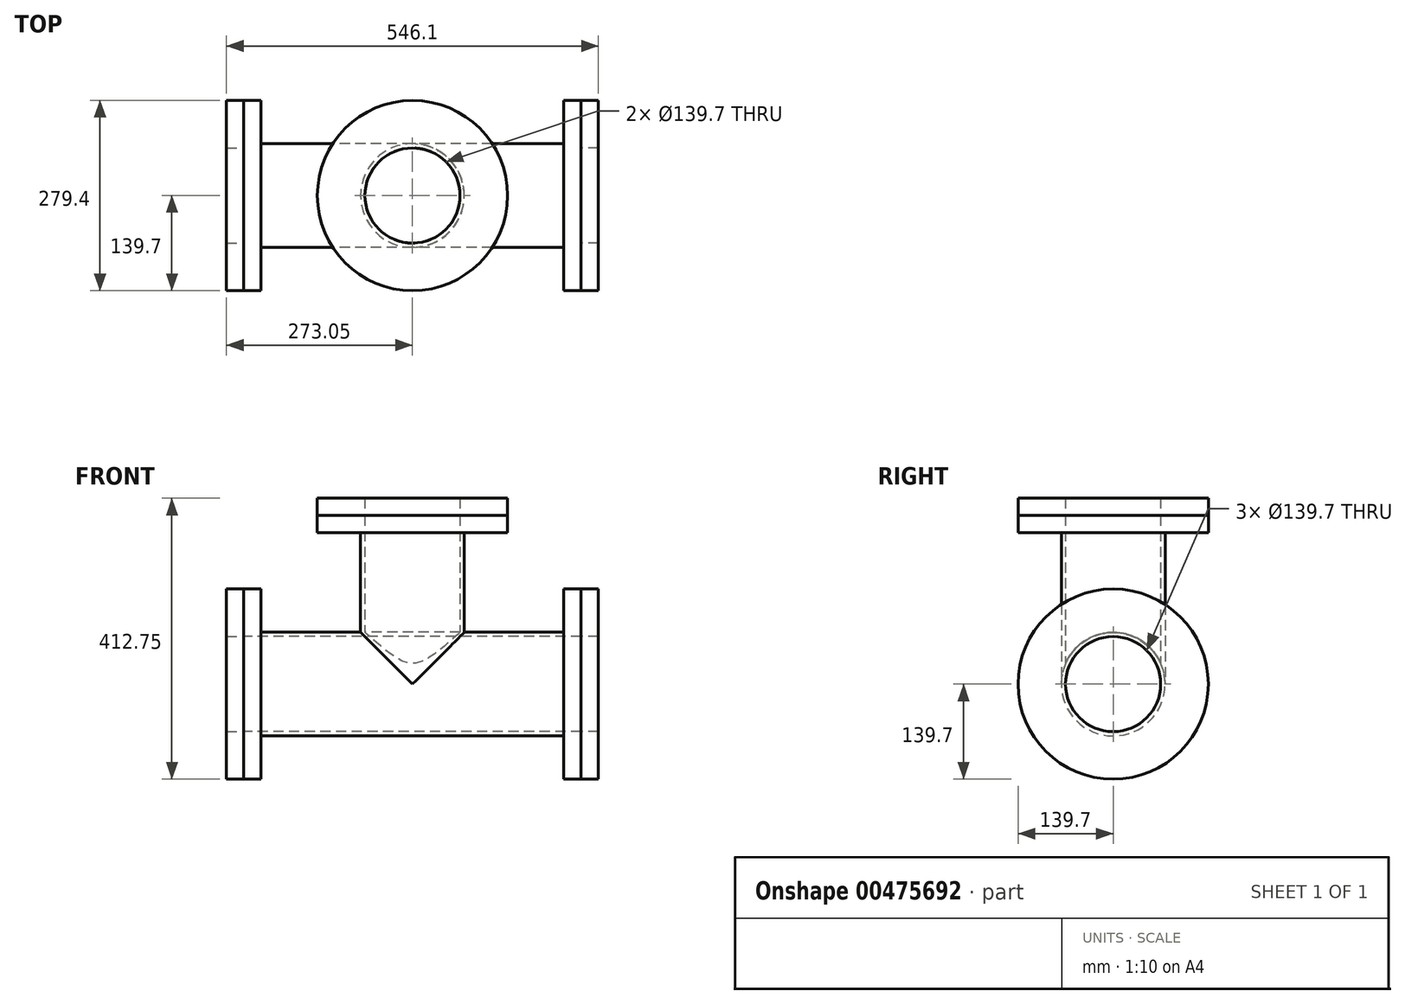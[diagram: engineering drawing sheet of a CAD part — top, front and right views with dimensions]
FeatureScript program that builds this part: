
annotation { "Feature Type Name" : "Feature", "Feature Type Description" : "" }
export const myFeature = defineFeature(function(context is Context, id is Id, definition is map)
    precondition{}
    {
        {
            var Q0;
            Q0=qCreatedBy(makeId("Top.planeOp"),FACE);
            var sketch = newSketch(context, id + "F0", { "sketchPlane" : qUnion([Q0])});
            skCircle(sketch, "E0", {"center": v(0, 0) * mm, "radius": 69.85 * mm});
            skCircle(sketch, "E1", {"center": v(0, 0) * mm, "radius": 76.2 * mm});
            skSolve(sketch);
        }
        {
            var Q0;
            Q0=makeQuery(id+"F0.imprint","IMPRINT",FACE,{"disambiguationData":[TD([[makeQuery(id+"F0.imprint","IMPRINT",EDGE,{"derivedFrom":sQuery(id+"F0.wireOp",EDGE,"E0")}),-1.0]])]});
            extrude(context, id + "F1", {"entities" : qUnion([Q0]), "depth" : 19.05 * mm});
        }
        {
            var Q0;
            Q0=makeQuery(id+"F1.opExtrude","CAP_FACE",FACE,{"disambiguationData":[OSD([sQuery(id+"F0.wireOp",EDGE,"E0"),sQuery(id+"F0.wireOp",EDGE,"E1")])],"isStart":false});
            var sketch = newSketch(context, id + "F2", { "sketchPlane" : qUnion([Q0])});
            skCircle(sketch, "E2", {"center": v(0, 0) * mm, "radius": 139.7 * mm});
            skSolve(sketch);
        }
        {
            var Q0;
            Q0=makeQuery(id+"F2.imprint","IMPRINT",FACE,{"disambiguationData":[TD([[makeQuery(id+"F2.imprint","IMPRINT",EDGE,{"derivedFrom":sQuery(id+"F2.wireOp",EDGE,"E2")}),1.0]])]});
            var Q1;
            Q1=makeQuery(id+"F2.imprint","IMPRINT",FACE,{"disambiguationData":[TD([[makeQuery(id+"F2.imprint","IMPRINT",EDGE,{"derivedFrom":makeQuery(id+"F1.opExtrude","CAP_EDGE",EDGE,{"disambiguationData":[OSD([sQuery(id+"F0.wireOp",EDGE,"E0")])],"isStart":false})}),-1.0]])]});
            extrude(context, id + "F3", {"entities" : qUnion([Q0, Q1]), "operationType" : NewBodyOperationType.ADD, "depth" : 25.4 * mm});
        }
        {
            var Q0;
            Q0=qCreatedBy(makeId("Front.planeOp"),FACE);
            var sketch = newSketch(context, id + "F4", { "sketchPlane" : qUnion([Q0])});
            skLineSegment(sketch, "E3", {"start": v(0, 0) * mm, "end": v(0, -50.8) * mm, "construction": true});
            skLineSegment(sketch, "E4", {"start": v(-152.4, -203.2) * mm, "end": v(-203.2, -203.2) * mm, "construction": true});
            skPoint(sketch, "E5.visualSharp", {"position": v(0, -203.2) * mm});
            skArc(sketch, "E5.filletArc", {"start": v(-152.4, -203.2) * mm, "mid": v(-44.64, -158.56) * mm, "end": v(0, -50.8) * mm, "construction": true});
            skArc(sketch, "E6.MirrorCS", {"start": v(152.4, -203.2) * mm, "mid": v(44.64, -158.56) * mm, "end": v(0, -50.8) * mm, "construction": true});
            skLineSegment(sketch, "E7.MirrorCS", {"start": v(152.4, -203.2) * mm, "end": v(203.2, -203.2) * mm, "construction": true});
            skSolve(sketch);
        }
        {
            var Q0;
            Q0=qCreatedBy(makeId("Front.planeOp"),FACE);
            var sketch = newSketch(context, id + "F5", { "sketchPlane" : qUnion([Q0])});
            skLineSegment(sketch, "E8", {"start": v(0, 0) * mm, "end": v(0, -172.58) * mm, "construction": true});
            skSolve(sketch);
        }
        {
            var Q0;
            Q0=qCreatedBy(makeId("Right.planeOp"),FACE);
            var Q1;
            Q1=sQuery(id+"F4.wireOp",VERTEX,"E7.MirrorCS.end");
            cPlane(context, id + "F6", {"entities" : qUnion([Q0, Q1]), "cplaneType" : CPlaneType.PLANE_POINT, "offset" : 25.4 * mm, "width" : 152.4 * mm, "height" : 152.4 * mm});
        }
        {
            var Q0;
            Q0=makeQuery(id+"F1.opExtrude","SWEPT_BODY",BODY,{"disambiguationData":[OSD([sQuery(id+"F0.wireOp",EDGE,"E0"),sQuery(id+"F0.wireOp",EDGE,"E1")])]});
            var Q1;
            Q1=sQuery(id+"F5.wireOp",VERTEX,"E8.start");
            var Q2;
            Q2=sQuery(id+"F4.wireOp",VERTEX,"E7.MirrorCS.end");
            transform(context, id + "F7", {"entities" : qUnion([Q0]), "transformType" : TransformType.TRANSLATION_ENTITY, "oppositeDirectionEntity" : false, "transformLine" : qUnion([Q1, Q2]), "makeCopy" : true});
        }
        {
            var Q0;
            Q0=qCreatedBy(id+"F6.planeOp",FACE);
            var sketch = newSketch(context, id + "F8", { "sketchPlane" : qUnion([Q0])});
            skLineSegment(sketch, "E9", {"start": v(-1.27, -203.2) * mm, "end": v(245.65, -203.2) * mm, "construction": true});
            skSolve(sketch);
        }
        {
            var Q0;
            Q0=makeQuery(id+"F7.opPattern","COPY",BODY,{"derivedFrom":makeQuery(id+"F1.opExtrude","SWEPT_BODY",BODY,{"disambiguationData":[OSD([sQuery(id+"F0.wireOp",EDGE,"E0"),sQuery(id+"F0.wireOp",EDGE,"E1")])]}),"instanceName":"1"});
            var Q1;
            Q1=sQuery(id+"F8.wireOp",EDGE,"E9");
            transform(context, id + "F9", {"entities" : qUnion([Q0]), "transformType" : TransformType.ROTATION, "transformAxis" : qUnion([Q1]), "angle" : 90 * degree, "makeCopy" : false});
        }
        {
            var Q0;
            Q0=makeQuery(id+"F7.opPattern","COPY",BODY,{"derivedFrom":makeQuery(id+"F1.opExtrude","SWEPT_BODY",BODY,{"disambiguationData":[OSD([sQuery(id+"F0.wireOp",EDGE,"E0"),sQuery(id+"F0.wireOp",EDGE,"E1")])]}),"instanceName":"1"});
            var Q1;
            Q1=qCreatedBy(makeId("Right.planeOp"),FACE);
            mirror(context, id + "F10", {"entities" : qUnion([Q0]), "mirrorPlane" : qUnion([Q1])});
        }
        {
            var Q0;
            Q0=makeQuery(id+"F7.opPattern","COPY",FACE,{"derivedFrom":makeQuery(id+"F1.opExtrude","CAP_FACE",FACE,{"disambiguationData":[OSD([sQuery(id+"F0.wireOp",EDGE,"E0"),sQuery(id+"F0.wireOp",EDGE,"E1")])],"isStart":true}),"instanceName":"1"});
            var Q1;
            Q1=makeQuery(id+"F10.opPattern","COPY",FACE,{"derivedFrom":makeQuery(id+"F7.opPattern","COPY",FACE,{"derivedFrom":makeQuery(id+"F1.opExtrude","CAP_FACE",FACE,{"disambiguationData":[OSD([sQuery(id+"F0.wireOp",EDGE,"E0"),sQuery(id+"F0.wireOp",EDGE,"E1")])],"isStart":true}),"instanceName":"1"}),"instanceName":"1"});
            extrude(context, id + "F11", {"entities" : qUnion([Q0]), "operationType" : NewBodyOperationType.ADD, "endBound" : BoundingType.UP_TO_SURFACE, "endBoundEntityFace" : qUnion([Q1]), "depth" : 25.4 * mm});
        }
        {
            var Q0;
            Q0=makeQuery(id+"F0.imprint","IMPRINT",FACE,{"disambiguationData":[TD([[makeQuery(id+"F0.imprint","IMPRINT",EDGE,{"derivedFrom":sQuery(id+"F0.wireOp",EDGE,"E0")}),-1.0]])]});
            var Q1;
            {var subQ0=sQuery(id+"F0.wireOp",EDGE,"E1");var subQ1=makeQuery(id+"F7.opPattern","COPY",FACE,{"derivedFrom":makeQuery(id+"F1.opExtrude","SWEPT_FACE",FACE,{"disambiguationData":[OSD([subQ0])]}),"instanceName":"1"});Q1=makeQuery(id+"F11.boolean.opBoolean","MERGE",FACE,{"derivedFrom":[subQ1,makeQuery(id+"F10.opPattern","COPY",FACE,{"derivedFrom":subQ1,"instanceName":"1"}),makeQuery(id+"F11.opExtrude","SWEPT_FACE",FACE,{"disambiguationData":[OSD([subQ0])]})]});}
            extrude(context, id + "F12", {"entities" : qUnion([Q0]), "operationType" : NewBodyOperationType.ADD, "endBound" : BoundingType.UP_TO_SURFACE, "oppositeDirection" : true, "endBoundEntityFace" : qUnion([Q1]), "depth" : 25.4 * mm});
        }
        {
            var Q0;
            Q0=makeQuery(id+"F3.opExtrude","CAP_FACE",FACE,{"disambiguationData":[OSD([sQuery(id+"F0.wireOp",EDGE,"E0"),sQuery(id+"F2.wireOp",EDGE,"E2")])],"isStart":false});
            extrude(context, id + "F13", {"entities" : qUnion([Q0]), "depth" : 25.4 * mm});
        }
        {
            var Q0;
            Q0=makeQuery(id+"F7.opPattern","COPY",FACE,{"derivedFrom":makeQuery(id+"F3.opExtrude","CAP_FACE",FACE,{"disambiguationData":[OSD([sQuery(id+"F0.wireOp",EDGE,"E0"),sQuery(id+"F2.wireOp",EDGE,"E2")])],"isStart":false}),"instanceName":"1"});
            extrude(context, id + "F14", {"entities" : qUnion([Q0]), "depth" : 25.4 * mm});
        }
        {
            var Q0;
            Q0=makeQuery(id+"F10.opPattern","COPY",FACE,{"derivedFrom":makeQuery(id+"F7.opPattern","COPY",FACE,{"derivedFrom":makeQuery(id+"F3.opExtrude","CAP_FACE",FACE,{"disambiguationData":[OSD([sQuery(id+"F0.wireOp",EDGE,"E0"),sQuery(id+"F2.wireOp",EDGE,"E2")])],"isStart":false}),"instanceName":"1"}),"instanceName":"1"});
            extrude(context, id + "F15", {"entities" : qUnion([Q0]), "depth" : 25.4 * mm});
        }
    });
